FCSTD DOCUMENT  (FreeCAD 0.16R6704 (Git))
Label: calibpattern_v3
License: All rights reserved
LicenseURL: http://en.wikipedia.org/wiki/All_rights_reserved
objects: Part::Part2DObjectPython×74, Sketcher::SketchObject×1, Spreadsheet::Sheet×1, Drawing::FeatureViewPart×1, Drawing::FeaturePage×1, Part::Feature×1
note: 76 computed .brp shape members not serialized (recipe doc carries the construction recipe); baked Part::Feature solids carry a one-line shape summary decoded from their .brp

FEATURE [Sketcher::SketchObject] Sketch
  expr: Constraints[197] = Data.r_Innerpattern
  expr: Constraints[128] = 5 * Data.alpha / 6
  expr: Constraints[31] = Data.s_small + 3 * (Data.s_big - Data.s_small) / 4
  expr: Constraints[24] = Data.alpha
  expr: Constraints[126] = 3 * Data.alpha / 6
  expr: Constraints[25] = Data.alpha
  expr: Constraints[30] = Data.s_small + 2 * (Data.s_big - Data.s_small) / 4
  expr: Constraints[27] = Data.alpha
  expr: Constraints[125] = 2 * Data.alpha / 6
  expr: Constraints[23] = Data.alpha
  expr: Constraints[32] = Data.s_small + 4 * (Data.s_big - Data.s_small) / 4
  expr: Constraints[88] = Data.r_pattern
  expr: Constraints[127] = 4 * Data.alpha / 6
  expr: Constraints[124] = Data.alpha / 6
  expr: Constraints[26] = Data.alpha
  expr: Constraints[29] = Data.s_small + (Data.s_big - Data.s_small) / 4
  sketch-geometry (82):
    g0: ArcOfCircle CenterX=0 CenterY=0 CenterZ=0 NormalX=0 NormalY=0 NormalZ=1 Radius=125.3 StartAngle=1.5708 EndAngle=4.57951
    g1: ArcOfCircle CenterX=0 CenterY=0 CenterZ=0 NormalX=0 NormalY=0 NormalZ=1 Radius=27.1483 StartAngle=1.5708 EndAngle=4.57951
    g2: Circle CenterX=0 CenterY=27.1483 CenterZ=0 NormalX=0 NormalY=0 NormalZ=1 Radius=2
    g3: Circle CenterX=0 CenterY=125.3 CenterZ=0 NormalX=0 NormalY=0 NormalZ=1 Radius=2
    g4: Circle CenterX=-60.2315 CenterY=109.873 CenterZ=0 NormalX=0 NormalY=0 NormalZ=1 Radius=2
    g5: Circle CenterX=-105.632 CenterY=67.393 CenterZ=0 NormalX=0 NormalY=0 NormalZ=1 Radius=2
    g6: Circle CenterX=-125.023 CenterY=8.31853 CenterZ=0 NormalX=0 NormalY=0 NormalZ=1 Radius=2
    g7: Circle CenterX=-13.0502 CenterY=23.8059 CenterZ=0 NormalX=0 NormalY=0 NormalZ=1 Radius=2
    g8: Circle CenterX=-22.887 CenterY=14.6018 CenterZ=0 NormalX=0 NormalY=0 NormalZ=1 Radius=2
    g9: Circle CenterX=-27.0884 CenterY=1.80235 CenterZ=0 NormalX=0 NormalY=0 NormalZ=1 Radius=2
    g10: Circle CenterX=-24.6198 CenterY=-11.4409 CenterZ=0 NormalX=0 NormalY=0 NormalZ=1 Radius=2
    g11: Circle CenterX=-16.0891 CenterY=-21.8671 CenterZ=0 NormalX=0 NormalY=0 NormalZ=1 Radius=2
    g12: Circle CenterX=-3.59675 CenterY=-26.9089 CenterZ=0 NormalX=0 NormalY=0 NormalZ=1 Radius=2
    g13: Circle CenterX=-113.63 CenterY=-52.8043 CenterZ=0 NormalX=0 NormalY=0 NormalZ=1 Radius=2
    g14: Circle CenterX=-74.2572 CenterY=-100.925 CenterZ=0 NormalX=0 NormalY=0 NormalZ=1 Radius=2
    g15: Circle CenterX=-16.6004 CenterY=-124.195 CenterZ=0 NormalX=0 NormalY=0 NormalZ=1 Radius=2
    g16: ArcOfCircle CenterX=0 CenterY=0 CenterZ=0 NormalX=0 NormalY=0 NormalZ=1 Radius=100.762 StartAngle=1.5708 EndAngle=4.57951
    g17: ArcOfCircle CenterX=0 CenterY=0 CenterZ=0 NormalX=0 NormalY=0 NormalZ=1 Radius=76.2239 StartAngle=1.5708 EndAngle=4.57951
    g18: ArcOfCircle CenterX=0 CenterY=0 CenterZ=0 NormalX=0 NormalY=0 NormalZ=1 Radius=51.6861 StartAngle=1.5708 EndAngle=4.57951
    g19: Circle CenterX=0 CenterY=100.762 CenterZ=0 NormalX=0 NormalY=0 NormalZ=1 Radius=2
    g20: Circle CenterX=-48.4362 CenterY=88.3565 CenterZ=0 NormalX=0 NormalY=0 NormalZ=1 Radius=2
    g21: Circle CenterX=-84.946 CenterY=54.1952 CenterZ=0 NormalX=0 NormalY=0 NormalZ=1 Radius=2
    g22: Circle CenterX=-100.539 CenterY=6.68949 CenterZ=0 NormalX=0 NormalY=0 NormalZ=1 Radius=2
    g23: Circle CenterX=-91.3772 CenterY=-42.4634 CenterZ=0 NormalX=0 NormalY=0 NormalZ=1 Radius=2
    g24: Circle CenterX=-59.7152 CenterY=-81.1606 CenterZ=0 NormalX=0 NormalY=0 NormalZ=1 Radius=2
    g25: Circle CenterX=-13.3495 CenterY=-99.8736 CenterZ=0 NormalX=0 NormalY=0 NormalZ=1 Radius=2
    g26: Circle CenterX=-10.0986 CenterY=-75.552 CenterZ=0 NormalX=0 NormalY=0 NormalZ=1 Radius=2
    g27: Circle CenterX=-6.84765 CenterY=-51.2305 CenterZ=0 NormalX=0 NormalY=0 NormalZ=1 Radius=2
    g28: Circle CenterX=-30.6311 CenterY=-41.6316 CenterZ=0 NormalX=0 NormalY=0 NormalZ=1 Radius=2
    g29: Circle CenterX=-45.1731 CenterY=-61.3961 CenterZ=0 NormalX=0 NormalY=0 NormalZ=1 Radius=2
    g30: Circle CenterX=-69.1247 CenterY=-32.1226 CenterZ=0 NormalX=0 NormalY=0 NormalZ=1 Radius=2
    g31: Circle CenterX=-46.8723 CenterY=-21.7818 CenterZ=0 NormalX=0 NormalY=0 NormalZ=1 Radius=2
    g32: Circle CenterX=-76.0558 CenterY=5.06044 CenterZ=0 NormalX=0 NormalY=0 NormalZ=1 Radius=2
    g33: Circle CenterX=-51.5721 CenterY=3.4314 CenterZ=0 NormalX=0 NormalY=0 NormalZ=1 Radius=2
    g34: Circle CenterX=-64.2596 CenterY=40.9974 CenterZ=0 NormalX=0 NormalY=0 NormalZ=1 Radius=2
    g35: Circle CenterX=-36.6408 CenterY=66.8396 CenterZ=0 NormalX=0 NormalY=0 NormalZ=1 Radius=2
    g36: Circle CenterX=0 CenterY=76.2239 CenterZ=0 NormalX=0 NormalY=0 NormalZ=1 Radius=2
    g37: Circle CenterX=0 CenterY=51.6861 CenterZ=0 NormalX=0 NormalY=0 NormalZ=1 Radius=2
    g38: Circle CenterX=-43.5733 CenterY=27.7996 CenterZ=0 NormalX=0 NormalY=0 NormalZ=1 Radius=2
    g39: Circle CenterX=-24.8455 CenterY=45.3228 CenterZ=0 NormalX=0 NormalY=0 NormalZ=1 Radius=2
    g40: LineSegment StartX=0 StartY=0 StartZ=0 EndX=-60.2315 EndY=109.873 EndZ=0
    g41: LineSegment StartX=0 StartY=125.3 StartZ=0 EndX=0 EndY=0 EndZ=0
    g42: LineSegment StartX=0 StartY=0 StartZ=0 EndX=-105.632 EndY=67.393 EndZ=0
    g43: LineSegment StartX=-125.023 StartY=8.31853 StartZ=0 EndX=0 EndY=0 EndZ=0
    g44: LineSegment StartX=0 StartY=0 StartZ=0 EndX=-113.63 EndY=-52.8043 EndZ=0
    g45: LineSegment StartX=-74.2572 StartY=-100.925 StartZ=0 EndX=0 EndY=0 EndZ=0
    g46: LineSegment StartX=0 StartY=0 StartZ=0 EndX=-16.6004 EndY=-124.195 EndZ=0
    g47: Circle CenterX=0 CenterY=76.2239 CenterZ=0 NormalX=0 NormalY=0 NormalZ=1 Radius=1
    g48: Circle CenterX=0 CenterY=100.762 CenterZ=0 NormalX=0 NormalY=0 NormalZ=1 Radius=1
    g49: Circle CenterX=0 CenterY=125.3 CenterZ=0 NormalX=0 NormalY=0 NormalZ=1 Radius=1
    g50: Circle CenterX=-60.2315 CenterY=109.873 CenterZ=0 NormalX=0 NormalY=0 NormalZ=1 Radius=1
    g51: Circle CenterX=-48.4362 CenterY=88.3565 CenterZ=0 NormalX=0 NormalY=0 NormalZ=1 Radius=1
    g52: Circle CenterX=-36.6408 CenterY=66.8396 CenterZ=0 NormalX=0 NormalY=0 NormalZ=1 Radius=1
    g53: Circle CenterX=-24.8455 CenterY=45.3228 CenterZ=0 NormalX=0 NormalY=0 NormalZ=1 Radius=1
    g54: Circle CenterX=0 CenterY=27.1483 CenterZ=0 NormalX=0 NormalY=0 NormalZ=1 Radius=1
    g55: Circle CenterX=-13.0502 CenterY=23.8059 CenterZ=0 NormalX=0 NormalY=0 NormalZ=1 Radius=1
    g56: Circle CenterX=-43.5733 CenterY=27.7996 CenterZ=0 NormalX=0 NormalY=0 NormalZ=1 Radius=1
    g57: Circle CenterX=-22.887 CenterY=14.6018 CenterZ=0 NormalX=0 NormalY=0 NormalZ=1 Radius=1
    g58: Circle CenterX=-64.2596 CenterY=40.9974 CenterZ=0 NormalX=0 NormalY=0 NormalZ=1 Radius=1
    g59: Circle CenterX=-84.946 CenterY=54.1952 CenterZ=0 NormalX=0 NormalY=0 NormalZ=1 Radius=1
    g60: Circle CenterX=-105.632 CenterY=67.393 CenterZ=0 NormalX=0 NormalY=0 NormalZ=1 Radius=1
    g61: Circle CenterX=-125.023 CenterY=8.31853 CenterZ=0 NormalX=0 NormalY=0 NormalZ=1 Radius=1
    g62: Circle CenterX=-100.539 CenterY=6.68949 CenterZ=0 NormalX=0 NormalY=0 NormalZ=1 Radius=1
    g63: Circle CenterX=-76.0558 CenterY=5.06044 CenterZ=0 NormalX=0 NormalY=0 NormalZ=1 Radius=1
    g64: Circle CenterX=-51.5721 CenterY=3.4314 CenterZ=0 NormalX=0 NormalY=0 NormalZ=1 Radius=1
    g65: Circle CenterX=-27.0884 CenterY=1.80235 CenterZ=0 NormalX=0 NormalY=0 NormalZ=1 Radius=1
    g66: Circle CenterX=-24.6198 CenterY=-11.4409 CenterZ=0 NormalX=0 NormalY=0 NormalZ=1 Radius=1
    g67: Circle CenterX=-46.8723 CenterY=-21.7818 CenterZ=0 NormalX=0 NormalY=0 NormalZ=1 Radius=1
    g68: Circle CenterX=-69.1247 CenterY=-32.1226 CenterZ=0 NormalX=0 NormalY=0 NormalZ=1 Radius=1
    g69: Circle CenterX=-91.3772 CenterY=-42.4634 CenterZ=0 NormalX=0 NormalY=0 NormalZ=1 Radius=1
    g70: Circle CenterX=-113.63 CenterY=-52.8043 CenterZ=0 NormalX=0 NormalY=0 NormalZ=1 Radius=1
    g71: Circle CenterX=-74.2572 CenterY=-100.925 CenterZ=0 NormalX=0 NormalY=0 NormalZ=1 Radius=1
    g72: Circle CenterX=-59.7152 CenterY=-81.1606 CenterZ=0 NormalX=0 NormalY=0 NormalZ=1 Radius=1
    g73: Circle CenterX=-45.1731 CenterY=-61.3961 CenterZ=0 NormalX=0 NormalY=0 NormalZ=1 Radius=1
    g74: Circle CenterX=-30.6311 CenterY=-41.6316 CenterZ=0 NormalX=0 NormalY=0 NormalZ=1 Radius=1
    g75: Circle CenterX=-16.0891 CenterY=-21.8671 CenterZ=0 NormalX=0 NormalY=0 NormalZ=1 Radius=1
    g76: Circle CenterX=-3.59675 CenterY=-26.9089 CenterZ=0 NormalX=0 NormalY=0 NormalZ=1 Radius=1
    g77: Circle CenterX=-6.84765 CenterY=-51.2305 CenterZ=0 NormalX=0 NormalY=0 NormalZ=1 Radius=1
    g78: Circle CenterX=-10.0986 CenterY=-75.552 CenterZ=0 NormalX=0 NormalY=0 NormalZ=1 Radius=1
    g79: Circle CenterX=-13.3495 CenterY=-99.8736 CenterZ=0 NormalX=0 NormalY=0 NormalZ=1 Radius=1
    g80: Circle CenterX=-16.6004 CenterY=-124.195 CenterZ=0 NormalX=0 NormalY=0 NormalZ=1 Radius=1
    g81: Circle CenterX=0 CenterY=51.6861 CenterZ=0 NormalX=0 NormalY=0 NormalZ=1 Radius=1
  constraints (198):
    c: PointOnObject(g0,g-2)
    c: Coincident(g0,g-1)
    c: Coincident(g1,g-1)
    c: Radius(g1) = 27.1483
    c: PointOnObject(g13,g0)
    c: PointOnObject(g5,g0)
    c: PointOnObject(g4,g0)
    c: PointOnObject(g14,g0)
    c: PointOnObject(g6,g0)
    c: Coincident(g2,g1)
    c: PointOnObject(g8,g1)
    c: Coincident(g12,g1)
    c: PointOnObject(g11,g1)
    c: PointOnObject(g9,g1)
    c: PointOnObject(g10,g1)
    c: Coincident(g15,g0)
    c: Coincident(g3,g0)
    c: Coincident(g16,g-1)
    c: PointOnObject(g16,g-2)
    c: Coincident(g17,g-1)
    c: PointOnObject(g17,g-2)
    c: Coincident(g18,g-1)
    c: PointOnObject(g18,g-2)
    c: Angle(g1) = 3.00872
    c: Angle(g18) = 3.00872
    c: Angle(g17) = 3.00872
    c: Angle(g16) = 3.00872
    c: Angle(g0) = 3.00872
    c: PointOnObject(g1,g-2)
    c: Radius(g18) = 51.6861
    c: Radius(g17) = 76.2239
    c: Radius(g16) = 100.762
    c: Radius(g0) = 125.3
    c: Coincident(g19,g16)
    c: PointOnObject(g20,g16)
    c: PointOnObject(g21,g16)
    c: PointOnObject(g22,g16)
    c: PointOnObject(g23,g16)
    c: PointOnObject(g24,g16)
    c: Coincident(g25,g16)
    c: Coincident(g26,g17)
    c: Coincident(g27,g18)
    c: PointOnObject(g28,g18)
    c: PointOnObject(g29,g17)
    c: PointOnObject(g30,g17)
    c: PointOnObject(g31,g18)
    c: PointOnObject(g32,g17)
    c: PointOnObject(g33,g18)
    c: PointOnObject(g34,g17)
    c: PointOnObject(g35,g17)
    c: Coincident(g36,g17)
    c: Coincident(g37,g18)
    c: PointOnObject(g38,g18)
    c: PointOnObject(g39,g18)
    c: Equal(g39,g37)
    c: Equal(g19,g20)
    c: Equal(g20,g21)
    c: Equal(g21,g22)
    c: Equal(g22,g23)
    c: Equal(g23,g24)
    c: Equal(g24,g25)
    c: Equal(g25,g26)
    c: Equal(g26,g27)
    c: Equal(g27,g28)
    c: Equal(g28,g29)
    c: Equal(g29,g30)
    c: Equal(g30,g31)
    c: Equal(g31,g32)
    c: Equal(g32,g33)
    c: Equal(g33,g34)
    c: Equal(g34,g35)
    c: Equal(g35,g36)
    c: Equal(g36,g37)
    c: Equal(g37,g38)
    c: Equal(g2,g3)
    c: Equal(g3,g4)
    c: Equal(g4,g5)
    c: Equal(g5,g6)
    c: Equal(g6,g7)
    c: Equal(g7,g8)
    c: Equal(g8,g9)
    c: Equal(g9,g10)
    c: Equal(g10,g11)
    c: Equal(g11,g12)
    c: Equal(g12,g13)
    c: Equal(g13,g14)
    c: Equal(g14,g15)
    c: Equal(g2,g37)
    c: Radius(g3) = 2
    c: Coincident(g40,g-1)
    c: Coincident(g40,g4)
    c: Coincident(g41,g0)
    c: Coincident(g41,g-1)
    c: Coincident(g42,g-1)
    c: Coincident(g42,g5)
    c: Coincident(g43,g6)
    c: Coincident(g43,g-1)
    c: Coincident(g44,g-1)
    c: Coincident(g44,g13)
    c: Coincident(g45,g14)
    c: Coincident(g45,g-1)
    c: Coincident(g46,g-1)
    c: Coincident(g46,g0)
    c: PointOnObject(g20,g40)
    c: PointOnObject(g39,g40)
    c: PointOnObject(g7,g40)
    c: PointOnObject(g7,g1)
    c: PointOnObject(g35,g40)
    c: PointOnObject(g21,g42)
    c: PointOnObject(g34,g42)
    c: PointOnObject(g38,g42)
    c: PointOnObject(g8,g42)
    c: PointOnObject(g22,g43)
    c: PointOnObject(g32,g43)
    c: PointOnObject(g9,g43)
    c: PointOnObject(g33,g43)
    c: PointOnObject(g10,g44)
    c: PointOnObject(g31,g44)
    c: PointOnObject(g30,g44)
    c: PointOnObject(g23,g44)
    c: PointOnObject(g24,g45)
    c: PointOnObject(g29,g45)
    c: PointOnObject(g28,g45)
    c: PointOnObject(g11,g45)
    c: Angle(g41,g40) = 0.501453
    c: Angle(g41,g42) = 1.00291
    c: Angle(g41,g43) = 1.50436
    c: Angle(g41,g44) = 2.00581
    c: Angle(g41,g45) = 2.50726
    c: Coincident(g47,g17)
    c: Coincident(g48,g16)
    c: Coincident(g49,g0)
    c: Coincident(g50,g4)
    c: Coincident(g51,g20)
    c: Coincident(g52,g35)
    c: Coincident(g53,g39)
    c: Coincident(g54,g1)
    c: Coincident(g55,g7)
    c: Coincident(g56,g38)
    c: Coincident(g57,g8)
    c: Coincident(g58,g34)
    c: Coincident(g59,g21)
    c: Coincident(g60,g5)
    c: Coincident(g61,g6)
    c: Coincident(g62,g22)
    c: Coincident(g63,g32)
    c: Coincident(g64,g33)
    c: Coincident(g66,g10)
    c: Coincident(g67,g31)
    c: Coincident(g68,g30)
    c: Coincident(g69,g23)
    c: Coincident(g70,g13)
    c: Coincident(g71,g14)
    c: Coincident(g72,g24)
    c: Coincident(g73,g29)
    c: Coincident(g74,g28)
    c: Coincident(g75,g11)
    c: Coincident(g76,g1)
    c: Coincident(g77,g18)
    c: Coincident(g78,g17)
    c: Coincident(g79,g16)
    c: Coincident(g80,g0)
    c: Coincident(g81,g18)
    c: Equal(g47,g48)
    c: Equal(g48,g49)
    c: Equal(g49,g50)
    c: Equal(g50,g51)
    c: Equal(g51,g52)
    c: Equal(g52,g53)
    c: Equal(g53,g54)
    c: Equal(g54,g55)
    c: Equal(g55,g56)
    c: Equal(g56,g57)
    c: Equal(g57,g58)
    c: Equal(g58,g59)
    c: Equal(g59,g60)
    c: Equal(g60,g61)
    c: Equal(g61,g62)
    c: Equal(g62,g63)
    c: Equal(g63,g64)
    c: Equal(g64,g65)
    c: Equal(g65,g66)
    c: Equal(g66,g67)
    c: Equal(g67,g68)
    c: Equal(g68,g69)
    c: Equal(g69,g70)
    c: Equal(g70,g71)
    c: Equal(g71,g72)
    c: Equal(g72,g73)
    c: Equal(g73,g74)
    c: Equal(g74,g75)
    c: Equal(g75,g76)
    c: Equal(g76,g77)
    c: Equal(g77,g78)
    c: Equal(g78,g79)
    c: Equal(g79,g80)
    c: Equal(g80,g81)
    c: Radius(g49) = 1
FEATURE [Spreadsheet::Sheet] Spreadsheet  label="Data"
  cells = A1=R; B1(r_big)=60; A2=r; B2(r_small)=13; A3=H; B3(h_big)=110; A4=rPattern; B4(r_pattern)=2; A5=rInnerPattern; B5(r_Innerpattern)=1; A9=calculated:; A10=S; B10(s_big)==sqrt(h_big * h_big + r_big * r_big); C10=whole cone outer; A11=alpha; B11(alpha)==360 * r_big / s_big; A12=h; B12(h_small)==h_big * r_small / r_big; C12=top cone outer; A13=s; B13(s_small)==sqrt(h_small * h_small + r_small * r_small); C13=top cone outer
FEATURE [Drawing::FeatureViewPart] Ortho  label="Ortho_0_0"
  Direction = (0,0,1)
  HiddenWidth = 0.15
  LineWidth = 0.5
  Rotation = 0
  ShowHiddenLines = false
  ShowSmoothLines = false
  Source = -> Sketch
  Tolerance = 0.05
  ViewResult = <blob: 2588 chars omitted>
  Visible = true
  X = 167.512
  Y = 149.052
FEATURE [Drawing::FeaturePage] Page
  Group = -> [Ortho]
FEATURE [Part::Feature] Sketch001
  shape: bbox 125.3 x 249.5 x 2e-07 mm, 0 faces, 0 solids (baked)
FEATURE [Part::Part2DObjectPython] Circle  # Draft 2D object (typed FeaturePython)
  FirstAngle = 90
  LastAngle = -97.6132
  MakeFace = false
  Radius = 27.1483
FEATURE [Part::Part2DObjectPython] Circle001  # Draft 2D object (typed FeaturePython)
  FirstAngle = 0
  LastAngle = 0
  MakeFace = false
  Placement = pos=(0,27.1483,0) rot=(0,0,1;0rad)
  Radius = 2
FEATURE [Part::Part2DObjectPython] Circle002  # Draft 2D object (typed FeaturePython)
  FirstAngle = 0
  LastAngle = 0
  MakeFace = false
  Placement = pos=(0,125.3,0) rot=(0,0,1;0rad)
  Radius = 2
FEATURE [Part::Part2DObjectPython] Circle003  # Draft 2D object (typed FeaturePython)
  FirstAngle = 0
  LastAngle = 0
  MakeFace = false
  Placement = pos=(-60.2315,109.873,0) rot=(0,0,1;0rad)
  Radius = 2
FEATURE [Part::Part2DObjectPython] Circle004  # Draft 2D object (typed FeaturePython)
  FirstAngle = 0
  LastAngle = 0
  MakeFace = false
  Placement = pos=(-105.632,67.393,0) rot=(0,0,1;0rad)
  Radius = 2
FEATURE [Part::Part2DObjectPython] Circle005  # Draft 2D object (typed FeaturePython)
  FirstAngle = 0
  LastAngle = 0
  MakeFace = false
  Placement = pos=(-125.023,8.31853,0) rot=(0,0,1;0rad)
  Radius = 2
FEATURE [Part::Part2DObjectPython] Circle006  # Draft 2D object (typed FeaturePython)
  FirstAngle = 0
  LastAngle = 0
  MakeFace = false
  Placement = pos=(-13.0502,23.8059,0) rot=(0,0,1;0rad)
  Radius = 2
FEATURE [Part::Part2DObjectPython] Circle007  # Draft 2D object (typed FeaturePython)
  FirstAngle = 0
  LastAngle = 0
  MakeFace = false
  Placement = pos=(-22.887,14.6018,0) rot=(0,0,1;0rad)
  Radius = 2
FEATURE [Part::Part2DObjectPython] Circle008  # Draft 2D object (typed FeaturePython)
  FirstAngle = 0
  LastAngle = 0
  MakeFace = false
  Placement = pos=(-27.0884,1.80235,0) rot=(0,0,1;0rad)
  Radius = 2
FEATURE [Part::Part2DObjectPython] Circle009  # Draft 2D object (typed FeaturePython)
  FirstAngle = 0
  LastAngle = 0
  MakeFace = false
  Placement = pos=(-24.6198,-11.4409,0) rot=(0,0,1;0rad)
  Radius = 2
FEATURE [Part::Part2DObjectPython] Circle010  # Draft 2D object (typed FeaturePython)
  FirstAngle = 0
  LastAngle = 0
  MakeFace = false
  Placement = pos=(-16.0891,-21.8671,0) rot=(0,0,1;0rad)
  Radius = 2
FEATURE [Part::Part2DObjectPython] Circle011  # Draft 2D object (typed FeaturePython)
  FirstAngle = 0
  LastAngle = 0
  MakeFace = false
  Placement = pos=(-3.59675,-26.9089,0) rot=(0,0,1;0rad)
  Radius = 2
FEATURE [Part::Part2DObjectPython] Circle012  # Draft 2D object (typed FeaturePython)
  FirstAngle = 0
  LastAngle = 0
  MakeFace = false
  Placement = pos=(-113.63,-52.8043,0) rot=(0,0,1;0rad)
  Radius = 2
FEATURE [Part::Part2DObjectPython] Circle013  # Draft 2D object (typed FeaturePython)
  FirstAngle = 0
  LastAngle = 0
  MakeFace = false
  Placement = pos=(-74.2572,-100.925,0) rot=(0,0,1;0rad)
  Radius = 2
FEATURE [Part::Part2DObjectPython] Circle014  # Draft 2D object (typed FeaturePython)
  FirstAngle = 0
  LastAngle = 0
  MakeFace = false
  Placement = pos=(-16.6004,-124.195,0) rot=(0,0,1;0rad)
  Radius = 2
FEATURE [Part::Part2DObjectPython] Circle015  # Draft 2D object (typed FeaturePython)
  FirstAngle = 90
  LastAngle = -97.6132
  MakeFace = false
  Radius = 100.762
FEATURE [Part::Part2DObjectPython] Circle016  # Draft 2D object (typed FeaturePython)
  FirstAngle = 90
  LastAngle = -97.6132
  MakeFace = false
  Radius = 76.2239
FEATURE [Part::Part2DObjectPython] Circle017  # Draft 2D object (typed FeaturePython)
  FirstAngle = 90
  LastAngle = -97.6132
  MakeFace = false
  Radius = 51.6861
FEATURE [Part::Part2DObjectPython] Circle018  # Draft 2D object (typed FeaturePython)
  FirstAngle = 0
  LastAngle = 0
  MakeFace = false
  Placement = pos=(0,100.762,0) rot=(0,0,1;0rad)
  Radius = 2
FEATURE [Part::Part2DObjectPython] Circle019  # Draft 2D object (typed FeaturePython)
  FirstAngle = 0
  LastAngle = 0
  MakeFace = false
  Placement = pos=(-48.4362,88.3565,0) rot=(0,0,1;0rad)
  Radius = 2
FEATURE [Part::Part2DObjectPython] Circle020  # Draft 2D object (typed FeaturePython)
  FirstAngle = 0
  LastAngle = 0
  MakeFace = false
  Placement = pos=(-84.946,54.1952,0) rot=(0,0,1;0rad)
  Radius = 2
FEATURE [Part::Part2DObjectPython] Circle021  # Draft 2D object (typed FeaturePython)
  FirstAngle = 0
  LastAngle = 0
  MakeFace = false
  Placement = pos=(-100.539,6.68949,0) rot=(0,0,1;0rad)
  Radius = 2
FEATURE [Part::Part2DObjectPython] Circle022  # Draft 2D object (typed FeaturePython)
  FirstAngle = 0
  LastAngle = 0
  MakeFace = false
  Placement = pos=(-91.3772,-42.4634,0) rot=(0,0,1;0rad)
  Radius = 2
FEATURE [Part::Part2DObjectPython] Circle023  # Draft 2D object (typed FeaturePython)
  FirstAngle = 0
  LastAngle = 0
  MakeFace = false
  Placement = pos=(-59.7152,-81.1606,0) rot=(0,0,1;0rad)
  Radius = 2
FEATURE [Part::Part2DObjectPython] Circle024  # Draft 2D object (typed FeaturePython)
  FirstAngle = 0
  LastAngle = 0
  MakeFace = false
  Placement = pos=(-13.3495,-99.8736,0) rot=(0,0,1;0rad)
  Radius = 2
FEATURE [Part::Part2DObjectPython] Circle025  # Draft 2D object (typed FeaturePython)
  FirstAngle = 0
  LastAngle = 0
  MakeFace = false
  Placement = pos=(-10.0986,-75.552,0) rot=(0,0,1;0rad)
  Radius = 2
FEATURE [Part::Part2DObjectPython] Circle026  # Draft 2D object (typed FeaturePython)
  FirstAngle = 0
  LastAngle = 0
  MakeFace = false
  Placement = pos=(-6.84765,-51.2305,0) rot=(0,0,1;0rad)
  Radius = 2
FEATURE [Part::Part2DObjectPython] Circle027  # Draft 2D object (typed FeaturePython)
  FirstAngle = 0
  LastAngle = 0
  MakeFace = false
  Placement = pos=(-30.6311,-41.6316,0) rot=(0,0,1;0rad)
  Radius = 2
FEATURE [Part::Part2DObjectPython] Circle028  # Draft 2D object (typed FeaturePython)
  FirstAngle = 0
  LastAngle = 0
  MakeFace = false
  Placement = pos=(-45.1731,-61.3961,0) rot=(0,0,1;0rad)
  Radius = 2
FEATURE [Part::Part2DObjectPython] Circle029  # Draft 2D object (typed FeaturePython)
  FirstAngle = 0
  LastAngle = 0
  MakeFace = false
  Placement = pos=(-69.1247,-32.1226,0) rot=(0,0,1;0rad)
  Radius = 2
FEATURE [Part::Part2DObjectPython] Circle030  # Draft 2D object (typed FeaturePython)
  FirstAngle = 0
  LastAngle = 0
  MakeFace = false
  Placement = pos=(-46.8723,-21.7818,0) rot=(0,0,1;0rad)
  Radius = 2
FEATURE [Part::Part2DObjectPython] Circle031  # Draft 2D object (typed FeaturePython)
  FirstAngle = 0
  LastAngle = 0
  MakeFace = false
  Placement = pos=(-76.0558,5.06044,0) rot=(0,0,1;0rad)
  Radius = 2
FEATURE [Part::Part2DObjectPython] Circle032  # Draft 2D object (typed FeaturePython)
  FirstAngle = 0
  LastAngle = 0
  MakeFace = false
  Placement = pos=(-51.5721,3.4314,0) rot=(0,0,1;0rad)
  Radius = 2
FEATURE [Part::Part2DObjectPython] Circle033  # Draft 2D object (typed FeaturePython)
  FirstAngle = 0
  LastAngle = 0
  MakeFace = false
  Placement = pos=(-64.2596,40.9974,0) rot=(0,0,1;0rad)
  Radius = 2
FEATURE [Part::Part2DObjectPython] Circle034  # Draft 2D object (typed FeaturePython)
  FirstAngle = 0
  LastAngle = 0
  MakeFace = false
  Placement = pos=(-36.6408,66.8396,0) rot=(0,0,1;0rad)
  Radius = 2
FEATURE [Part::Part2DObjectPython] Circle035  # Draft 2D object (typed FeaturePython)
  FirstAngle = 0
  LastAngle = 0
  MakeFace = false
  Placement = pos=(0,76.2239,0) rot=(0,0,1;0rad)
  Radius = 2
FEATURE [Part::Part2DObjectPython] Circle036  # Draft 2D object (typed FeaturePython)
  FirstAngle = 0
  LastAngle = 0
  MakeFace = false
  Placement = pos=(0,51.6861,0) rot=(0,0,1;0rad)
  Radius = 2
FEATURE [Part::Part2DObjectPython] Circle037  # Draft 2D object (typed FeaturePython)
  FirstAngle = 0
  LastAngle = 0
  MakeFace = false
  Placement = pos=(-43.5733,27.7996,0) rot=(0,0,1;0rad)
  Radius = 2
FEATURE [Part::Part2DObjectPython] Circle038  # Draft 2D object (typed FeaturePython)
  FirstAngle = 0
  LastAngle = 0
  MakeFace = false
  Placement = pos=(-24.8455,45.3228,0) rot=(0,0,1;0rad)
  Radius = 2
FEATURE [Part::Part2DObjectPython] Circle039  # Draft 2D object (typed FeaturePython)
  FirstAngle = 0
  LastAngle = 0
  MakeFace = false
  Placement = pos=(0,76.2239,0) rot=(0,0,1;0rad)
  Radius = 1
FEATURE [Part::Part2DObjectPython] Circle040  # Draft 2D object (typed FeaturePython)
  FirstAngle = 0
  LastAngle = 0
  MakeFace = false
  Placement = pos=(0,100.762,0) rot=(0,0,1;0rad)
  Radius = 1
FEATURE [Part::Part2DObjectPython] Circle041  # Draft 2D object (typed FeaturePython)
  FirstAngle = 0
  LastAngle = 0
  MakeFace = false
  Placement = pos=(0,125.3,0) rot=(0,0,1;0rad)
  Radius = 1
FEATURE [Part::Part2DObjectPython] Circle042  # Draft 2D object (typed FeaturePython)
  FirstAngle = 0
  LastAngle = 0
  MakeFace = false
  Placement = pos=(-60.2315,109.873,0) rot=(0,0,1;0rad)
  Radius = 1
FEATURE [Part::Part2DObjectPython] Circle043  # Draft 2D object (typed FeaturePython)
  FirstAngle = 0
  LastAngle = 0
  MakeFace = false
  Placement = pos=(-48.4362,88.3565,0) rot=(0,0,1;0rad)
  Radius = 1
FEATURE [Part::Part2DObjectPython] Circle044  # Draft 2D object (typed FeaturePython)
  FirstAngle = 0
  LastAngle = 0
  MakeFace = false
  Placement = pos=(-36.6408,66.8396,0) rot=(0,0,1;0rad)
  Radius = 1
FEATURE [Part::Part2DObjectPython] Circle045  # Draft 2D object (typed FeaturePython)
  FirstAngle = 0
  LastAngle = 0
  MakeFace = false
  Placement = pos=(-24.8455,45.3228,0) rot=(0,0,1;0rad)
  Radius = 1
FEATURE [Part::Part2DObjectPython] Circle046  # Draft 2D object (typed FeaturePython)
  FirstAngle = 0
  LastAngle = 0
  MakeFace = false
  Placement = pos=(0,27.1483,0) rot=(0,0,1;0rad)
  Radius = 1
FEATURE [Part::Part2DObjectPython] Circle047  # Draft 2D object (typed FeaturePython)
  FirstAngle = 0
  LastAngle = 0
  MakeFace = false
  Placement = pos=(-13.0502,23.8059,0) rot=(0,0,1;0rad)
  Radius = 1
FEATURE [Part::Part2DObjectPython] Circle048  # Draft 2D object (typed FeaturePython)
  FirstAngle = 0
  LastAngle = 0
  MakeFace = false
  Placement = pos=(-43.5733,27.7996,0) rot=(0,0,1;0rad)
  Radius = 1
FEATURE [Part::Part2DObjectPython] Circle049  # Draft 2D object (typed FeaturePython)
  FirstAngle = 0
  LastAngle = 0
  MakeFace = false
  Placement = pos=(-22.887,14.6018,0) rot=(0,0,1;0rad)
  Radius = 1
FEATURE [Part::Part2DObjectPython] Circle050  # Draft 2D object (typed FeaturePython)
  FirstAngle = 0
  LastAngle = 0
  MakeFace = false
  Placement = pos=(-64.2596,40.9974,0) rot=(0,0,1;0rad)
  Radius = 1
FEATURE [Part::Part2DObjectPython] Circle051  # Draft 2D object (typed FeaturePython)
  FirstAngle = 0
  LastAngle = 0
  MakeFace = false
  Placement = pos=(-84.946,54.1952,0) rot=(0,0,1;0rad)
  Radius = 1
FEATURE [Part::Part2DObjectPython] Circle052  # Draft 2D object (typed FeaturePython)
  FirstAngle = 0
  LastAngle = 0
  MakeFace = false
  Placement = pos=(-105.632,67.393,0) rot=(0,0,1;0rad)
  Radius = 1
FEATURE [Part::Part2DObjectPython] Circle053  # Draft 2D object (typed FeaturePython)
  FirstAngle = 0
  LastAngle = 0
  MakeFace = false
  Placement = pos=(-125.023,8.31853,0) rot=(0,0,1;0rad)
  Radius = 1
FEATURE [Part::Part2DObjectPython] Circle054  # Draft 2D object (typed FeaturePython)
  FirstAngle = 0
  LastAngle = 0
  MakeFace = false
  Placement = pos=(-100.539,6.68949,0) rot=(0,0,1;0rad)
  Radius = 1
FEATURE [Part::Part2DObjectPython] Circle055  # Draft 2D object (typed FeaturePython)
  FirstAngle = 0
  LastAngle = 0
  MakeFace = false
  Placement = pos=(-76.0558,5.06044,0) rot=(0,0,1;0rad)
  Radius = 1
FEATURE [Part::Part2DObjectPython] Circle056  # Draft 2D object (typed FeaturePython)
  FirstAngle = 0
  LastAngle = 0
  MakeFace = false
  Placement = pos=(-51.5721,3.4314,0) rot=(0,0,1;0rad)
  Radius = 1
FEATURE [Part::Part2DObjectPython] Circle057  # Draft 2D object (typed FeaturePython)
  FirstAngle = 0
  LastAngle = 0
  MakeFace = false
  Placement = pos=(-27.0884,1.80235,0) rot=(0,0,1;0rad)
  Radius = 1
FEATURE [Part::Part2DObjectPython] Circle058  # Draft 2D object (typed FeaturePython)
  FirstAngle = 0
  LastAngle = 0
  MakeFace = false
  Placement = pos=(-24.6198,-11.4409,0) rot=(0,0,1;0rad)
  Radius = 1
FEATURE [Part::Part2DObjectPython] Circle059  # Draft 2D object (typed FeaturePython)
  FirstAngle = 0
  LastAngle = 0
  MakeFace = false
  Placement = pos=(-46.8723,-21.7818,0) rot=(0,0,1;0rad)
  Radius = 1
FEATURE [Part::Part2DObjectPython] Circle060  # Draft 2D object (typed FeaturePython)
  FirstAngle = 0
  LastAngle = 0
  MakeFace = false
  Placement = pos=(-69.1247,-32.1226,0) rot=(0,0,1;0rad)
  Radius = 1
FEATURE [Part::Part2DObjectPython] Circle061  # Draft 2D object (typed FeaturePython)
  FirstAngle = 0
  LastAngle = 0
  MakeFace = false
  Placement = pos=(-91.3772,-42.4634,0) rot=(0,0,1;0rad)
  Radius = 1
FEATURE [Part::Part2DObjectPython] Circle062  # Draft 2D object (typed FeaturePython)
  FirstAngle = 0
  LastAngle = 0
  MakeFace = false
  Placement = pos=(-113.63,-52.8043,0) rot=(0,0,1;0rad)
  Radius = 1
FEATURE [Part::Part2DObjectPython] Circle063  # Draft 2D object (typed FeaturePython)
  FirstAngle = 0
  LastAngle = 0
  MakeFace = false
  Placement = pos=(-74.2572,-100.925,0) rot=(0,0,1;0rad)
  Radius = 1
FEATURE [Part::Part2DObjectPython] Circle064  # Draft 2D object (typed FeaturePython)
  FirstAngle = 0
  LastAngle = 0
  MakeFace = false
  Placement = pos=(-59.7152,-81.1606,0) rot=(0,0,1;0rad)
  Radius = 1
FEATURE [Part::Part2DObjectPython] Circle065  # Draft 2D object (typed FeaturePython)
  FirstAngle = 0
  LastAngle = 0
  MakeFace = false
  Placement = pos=(-45.1731,-61.3961,0) rot=(0,0,1;0rad)
  Radius = 1
FEATURE [Part::Part2DObjectPython] Circle066  # Draft 2D object (typed FeaturePython)
  FirstAngle = 0
  LastAngle = 0
  MakeFace = false
  Placement = pos=(-30.6311,-41.6316,0) rot=(0,0,1;0rad)
  Radius = 1
FEATURE [Part::Part2DObjectPython] Circle067  # Draft 2D object (typed FeaturePython)
  FirstAngle = 0
  LastAngle = 0
  MakeFace = false
  Placement = pos=(-16.0891,-21.8671,0) rot=(0,0,1;0rad)
  Radius = 1
FEATURE [Part::Part2DObjectPython] Circle068  # Draft 2D object (typed FeaturePython)
  FirstAngle = 0
  LastAngle = 0
  MakeFace = false
  Placement = pos=(-3.59675,-26.9089,0) rot=(0,0,1;0rad)
  Radius = 1
FEATURE [Part::Part2DObjectPython] Circle069  # Draft 2D object (typed FeaturePython)
  FirstAngle = 0
  LastAngle = 0
  MakeFace = false
  Placement = pos=(-6.84765,-51.2305,0) rot=(0,0,1;0rad)
  Radius = 1
FEATURE [Part::Part2DObjectPython] Circle070  # Draft 2D object (typed FeaturePython)
  FirstAngle = 0
  LastAngle = 0
  MakeFace = false
  Placement = pos=(-10.0986,-75.552,0) rot=(0,0,1;0rad)
  Radius = 1
FEATURE [Part::Part2DObjectPython] Circle071  # Draft 2D object (typed FeaturePython)
  FirstAngle = 0
  LastAngle = 0
  MakeFace = false
  Placement = pos=(-13.3495,-99.8736,0) rot=(0,0,1;0rad)
  Radius = 1
FEATURE [Part::Part2DObjectPython] Circle072  # Draft 2D object (typed FeaturePython)
  FirstAngle = 0
  LastAngle = 0
  MakeFace = false
  Placement = pos=(-16.6004,-124.195,0) rot=(0,0,1;0rad)
  Radius = 1
FEATURE [Part::Part2DObjectPython] Circle073  # Draft 2D object (typed FeaturePython)
  FirstAngle = 0
  LastAngle = 0
  MakeFace = false
  Placement = pos=(0,51.6861,0) rot=(0,0,1;0rad)
  Radius = 1
